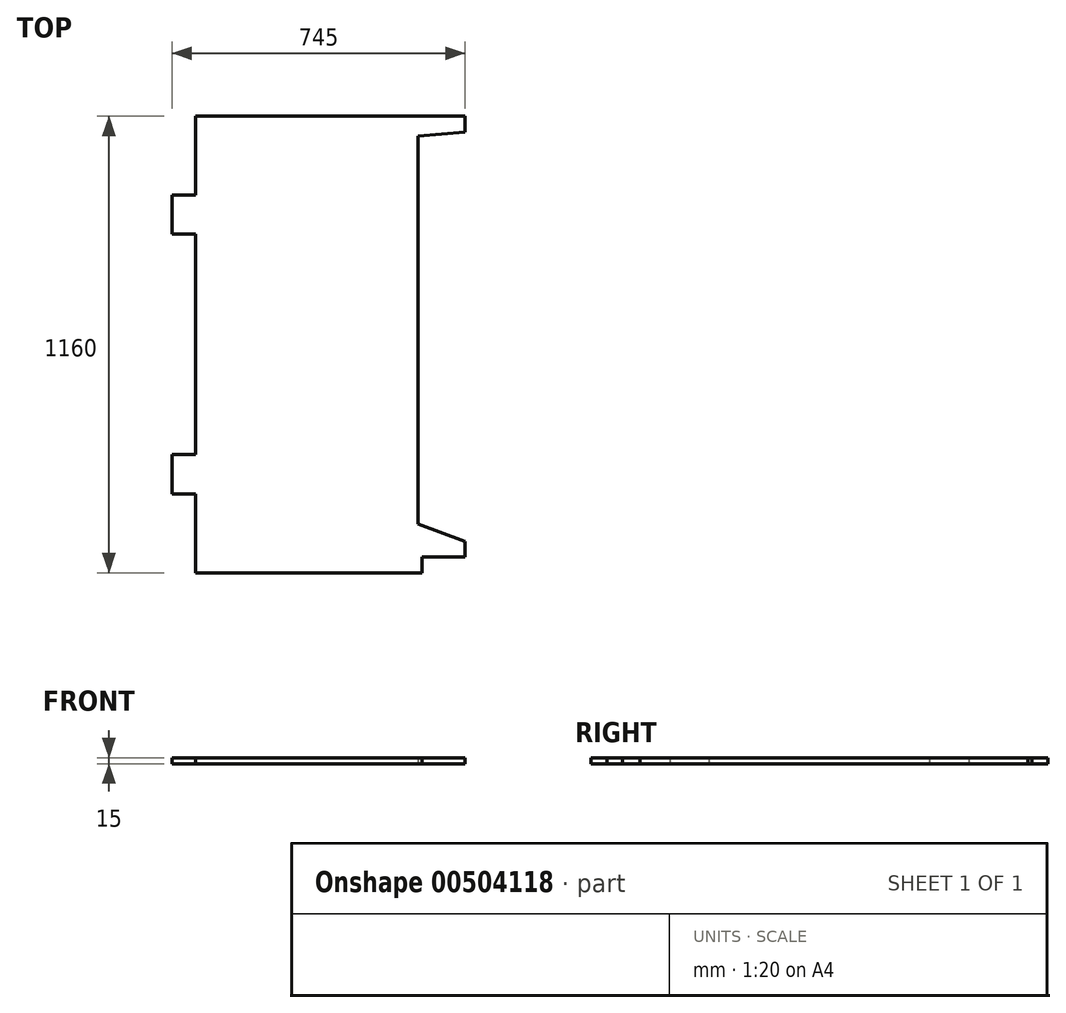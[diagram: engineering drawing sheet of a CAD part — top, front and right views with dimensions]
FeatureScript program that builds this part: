
annotation { "Feature Type Name" : "Feature", "Feature Type Description" : "" }
export const myFeature = defineFeature(function(context is Context, id is Id, definition is map)
    precondition{}
    {
        {
            var Q0;
            Q0=qCreatedBy(makeId("Top.planeOp"),FACE);
            var sketch = newSketch(context, id + "F0", { "sketchPlane" : qUnion([Q0])});
            skLineSegment(sketch, "E0", {"start": v(0, 0) * mm, "end": v(575, 0) * mm});
            skLineSegment(sketch, "E1", {"start": v(575, 0) * mm, "end": v(575, 40) * mm});
            skLineSegment(sketch, "E2", {"start": v(685, 40) * mm, "end": v(575, 40) * mm});
            skLineSegment(sketch, "E3", {"start": v(685, 40) * mm, "end": v(685, 80) * mm});
            skLineSegment(sketch, "E4", {"start": v(565, 123.68) * mm, "end": v(685, 80) * mm});
            skLineSegment(sketch, "E5", {"start": v(565, 123.68) * mm, "end": v(565, 1109.5) * mm});
            skLineSegment(sketch, "E6", {"start": v(565, 1109.5) * mm, "end": v(685, 1120) * mm});
            skLineSegment(sketch, "E7", {"start": v(685, 1120) * mm, "end": v(685, 1160) * mm});
            skLineSegment(sketch, "E8", {"start": v(685, 1160) * mm, "end": v(0, 1160) * mm});
            skLineSegment(sketch, "E9", {"start": v(0, 1160) * mm, "end": v(0, 960) * mm});
            skLineSegment(sketch, "E10", {"start": v(-60, 960) * mm, "end": v(0, 960) * mm});
            skLineSegment(sketch, "E11", {"start": v(-60, 960) * mm, "end": v(-60, 860) * mm});
            skLineSegment(sketch, "E12", {"start": v(0, 860) * mm, "end": v(-60, 860) * mm});
            skLineSegment(sketch, "E13", {"start": v(0, 860) * mm, "end": v(0, 300) * mm});
            skLineSegment(sketch, "E14", {"start": v(-60, 300) * mm, "end": v(0, 300) * mm});
            skLineSegment(sketch, "E15", {"start": v(-60, 300) * mm, "end": v(-60, 200) * mm});
            skLineSegment(sketch, "E16", {"start": v(0, 200) * mm, "end": v(-60, 200) * mm});
            skLineSegment(sketch, "E17", {"start": v(0, 200) * mm, "end": v(0, 0) * mm});
            skSolve(sketch);
        }
        {
            var Q0;
            Q0=makeQuery(id+"F0.imprint","IMPRINT",FACE,{"disambiguationData":[TD([[makeQuery(id+"F0.imprint","IMPRINT",EDGE,{"derivedFrom":sQuery(id+"F0.wireOp",EDGE,"E0")}),1.0]])]});
            extrude(context, id + "F1", {"entities" : qUnion([Q0]), "depth" : 15 * mm});
        }
    });
